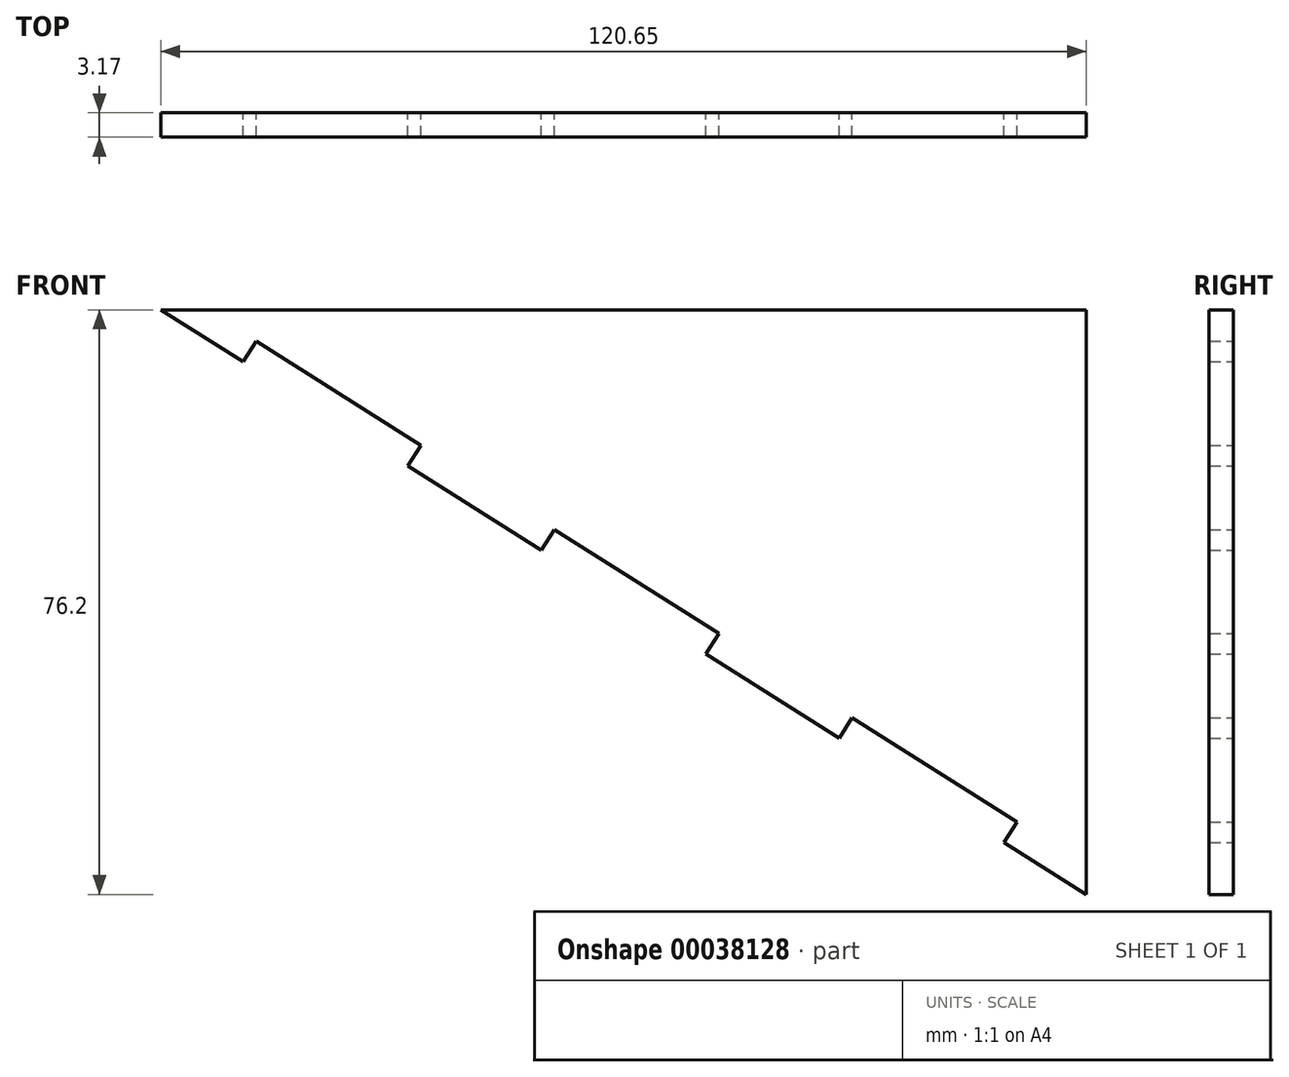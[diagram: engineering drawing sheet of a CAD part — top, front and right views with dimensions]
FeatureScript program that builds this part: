
annotation { "Feature Type Name" : "Feature", "Feature Type Description" : "" }
export const myFeature = defineFeature(function(context is Context, id is Id, definition is map)
    precondition{}
    {
        {
            var Q0;
            Q0=qCreatedBy(makeId("Front.planeOp"),FACE);
            var sketch = newSketch(context, id + "F0", { "sketchPlane" : qUnion([Q0])});
            skLineSegment(sketch, "E0", {"start": v(-62.93, 0) * mm, "end": v(57.72, 0) * mm});
            skLineSegment(sketch, "E1", {"start": v(57.72, 0) * mm, "end": v(57.72, -76.2) * mm});
            skLineSegment(sketch, "E2", {"start": v(-62.93, 0) * mm, "end": v(57.72, -76.2) * mm});
            skLineSegment(sketch, "E3", {"start": v(46.98, -69.42) * mm, "end": v(48.68, -66.73) * mm});
            skLineSegment(sketch, "E4", {"start": v(48.68, -66.73) * mm, "end": v(27.2, -53.17) * mm});
            skLineSegment(sketch, "E5", {"start": v(27.2, -53.17) * mm, "end": v(25.5, -55.85) * mm});
            skLineSegment(sketch, "E6", {"start": v(-52.2, -6.78) * mm, "end": v(-50.5, -4.1) * mm});
            skLineSegment(sketch, "E7", {"start": v(-50.5, -4.1) * mm, "end": v(-29.02, -17.66) * mm});
            skLineSegment(sketch, "E8", {"start": v(-29.02, -17.66) * mm, "end": v(-30.72, -20.35) * mm});
            skLineSegment(sketch, "E9", {"start": v(27.2, -53.17) * mm, "end": v(-29.02, -17.66) * mm, "construction": true});
            skLineSegment(sketch, "E10", {"start": v(-0.9, -35.42) * mm, "end": v(-2.6, -38.1) * mm, "construction": true});
            skLineSegment(sketch, "E11", {"start": v(8.13, -44.88) * mm, "end": v(9.83, -42.2) * mm});
            skLineSegment(sketch, "E12", {"start": v(9.83, -42.2) * mm, "end": v(-0.9, -35.42) * mm});
            skLineSegment(sketch, "E13", {"start": v(-13.34, -31.32) * mm, "end": v(-11.65, -28.63) * mm});
            skLineSegment(sketch, "E14", {"start": v(-11.65, -28.63) * mm, "end": v(-0.9, -35.42) * mm});
            skSolve(sketch);
        }
        {
            var Q0;
            {var subQ1=sQuery(id+"F0.wireOp",EDGE,"04dce7f2-cdfa-44ef-a768-ff4a84fa187b");Q0=makeQuery(id+"F0.imprint","IMPRINT",FACE,{"disambiguationData":[TD([[makeQuery(id+"F0.imprint","IMPRINT",EDGE,{"derivedFrom":subQ1}),1.0]])]});}
            var Q1;
            {var subQ1=sQuery(id+"F0.wireOp",EDGE,"E1");Q1=makeQuery(id+"F0.imprint","IMPRINT",FACE,{"disambiguationData":[TD([[makeQuery(id+"F0.imprint","IMPRINT",EDGE,{"derivedFrom":subQ1}),-1.0]])]});}
            var Q2;
            {var subQ1=sQuery(id+"F0.wireOp",EDGE,"d907eb41-dbe8-44e7-84e3-b7214bfe3bd9");Q2=makeQuery(id+"F0.imprint","IMPRINT",FACE,{"disambiguationData":[TD([[makeQuery(id+"F0.imprint","IMPRINT",EDGE,{"derivedFrom":subQ1}),-1.0]])]});}
            extrude(context, id + "F1", {"entities" : qUnion([Q0, Q1, Q2]), "depth" : 3.17 * mm});
        }
    });
